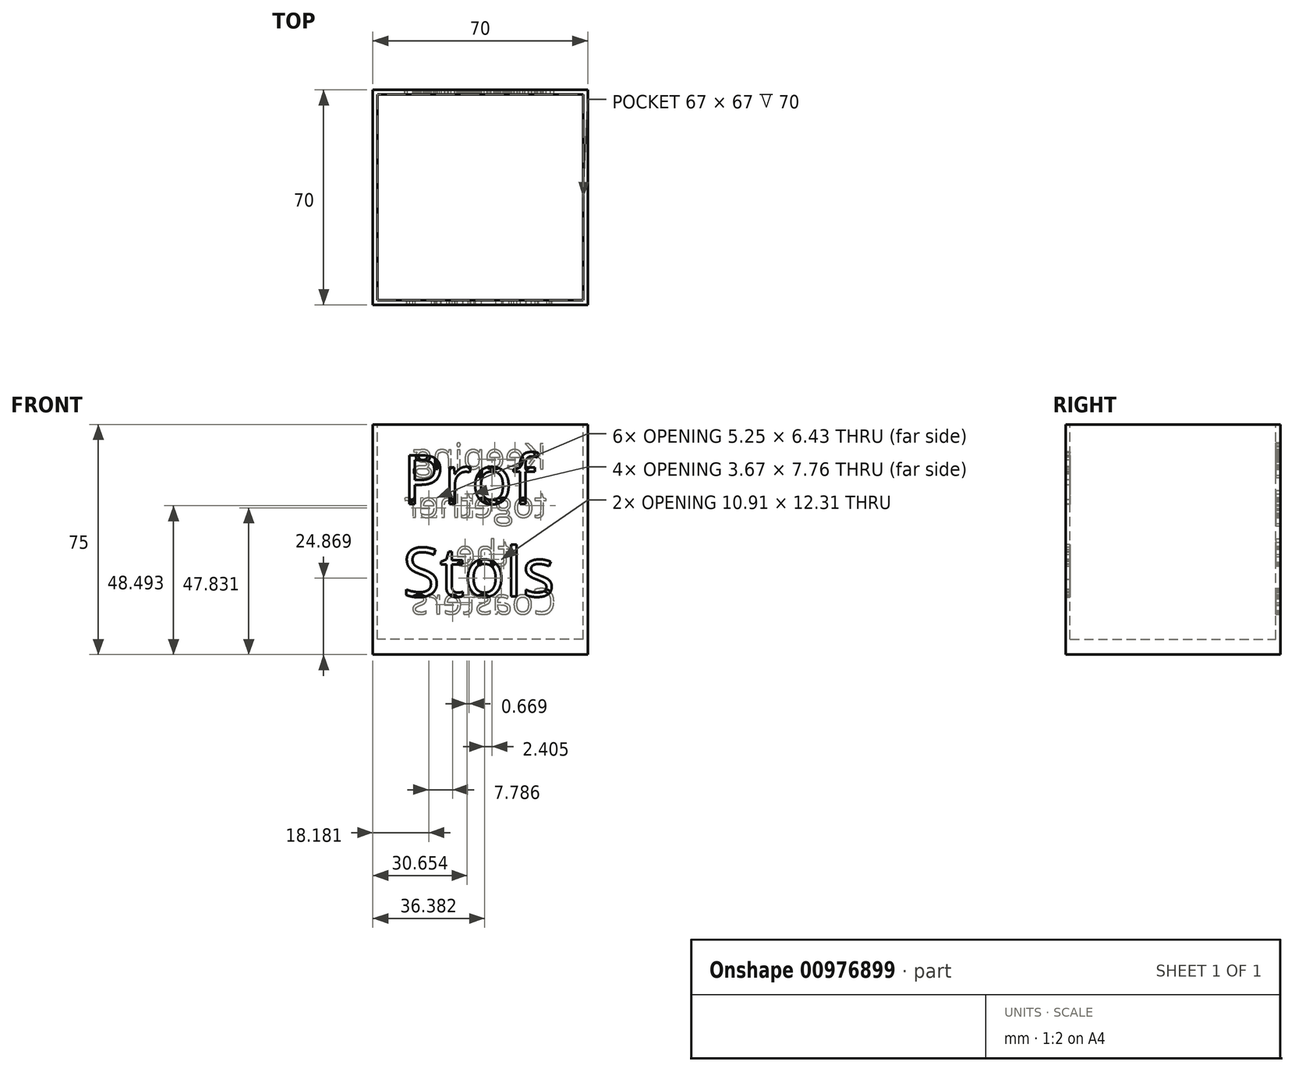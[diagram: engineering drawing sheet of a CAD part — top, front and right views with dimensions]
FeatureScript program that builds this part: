
annotation { "Feature Type Name" : "Feature", "Feature Type Description" : "" }
export const myFeature = defineFeature(function(context is Context, id is Id, definition is map)
    precondition{}
    {
        {
            var Q0;
            Q0=qCreatedBy(makeId("Top.planeOp"),FACE);
            var sketch = newSketch(context, id + "F0", { "sketchPlane" : qUnion([Q0])});
            skLineSegment(sketch, "E0.bottom", {"start": v(35, -35) * mm, "end": v(-35, -35) * mm});
            skLineSegment(sketch, "E0.top", {"start": v(35, 35) * mm, "end": v(-35, 35) * mm});
            skLineSegment(sketch, "E0.left", {"start": v(35, -35) * mm, "end": v(35, 35) * mm});
            skLineSegment(sketch, "E0.right", {"start": v(-35, -35) * mm, "end": v(-35, 35) * mm});
            skPoint(sketch, "E0.middle", {"position": v(0, 0) * mm});
            skSolve(sketch);
        }
        {
            var Q0;
            Q0 = qSketchRegion(id + "F0", true);
            extrude(context, id + "F1", {"entities" : qUnion([Q0]), "depth" : 75 * mm, "offsetDistance" : 25 * mm});
        }
        {
            var Q0;
            Q0=makeQuery(id+"F1.opExtrude","CAP_FACE",FACE,{"disambiguationData":[OSD([sQuery(id+"F0.wireOp",EDGE,"E0.bottom"),sQuery(id+"F0.wireOp",EDGE,"E0.top"),sQuery(id+"F0.wireOp",EDGE,"E0.left"),sQuery(id+"F0.wireOp",EDGE,"E0.right")])],"isStart":false});
            var sketch = newSketch(context, id + "F2", { "sketchPlane" : qUnion([Q0])});
            skLineSegment(sketch, "E1.bottom", {"start": v(33.5, -33.5) * mm, "end": v(-33.5, -33.5) * mm});
            skLineSegment(sketch, "E1.top", {"start": v(33.5, 33.5) * mm, "end": v(-33.5, 33.5) * mm});
            skLineSegment(sketch, "E1.left", {"start": v(33.5, -33.5) * mm, "end": v(33.5, 33.5) * mm});
            skLineSegment(sketch, "E1.right", {"start": v(-33.5, -33.5) * mm, "end": v(-33.5, 33.5) * mm});
            skPoint(sketch, "E1.middle", {"position": v(0, 0) * mm});
            skSolve(sketch);
        }
        {
            var Q0;
            Q0 = qSketchRegion(id + "F2", true);
            extrude(context, id + "F3", {"entities" : qUnion([Q0]), "operationType" : NewBodyOperationType.REMOVE, "oppositeDirection" : true, "depth" : 70 * mm, "offsetDistance" : 25 * mm});
        }
        {
            var Q0;
            Q0=makeQuery(id+"F1.opExtrude","SWEPT_FACE",FACE,{"disambiguationData":[OSD([sQuery(id+"F0.wireOp",EDGE,"E0.bottom")])]});
            var sketch = newSketch(context, id + "F4", { "sketchPlane" : qUnion([Q0])});
            skText(sketch, "E2", { "text": "Prof \nStols", "fontName": "OpenSans-Regular.ttf"});
            const initialGuessF4  = {"E2": [-0.02532, 0.0491, 1, 0, 0.01597]};
            skSetInitialGuess(sketch, initialGuessF4);
            skSolve(sketch);
        }
        {
            var Q0;
            Q0 = qSketchRegion(id + "F4", true);
            extrude(context, id + "F5", {"entities" : qUnion([Q0]), "operationType" : NewBodyOperationType.REMOVE, "oppositeDirection" : true, "depth" : 5 * mm, "offsetDistance" : 25 * mm});
        }
        {
            var Q0;
            Q0=makeQuery(id+"F1.opExtrude","SWEPT_FACE",FACE,{"disambiguationData":[OSD([sQuery(id+"F0.wireOp",EDGE,"E0.top")])]});
            var sketch = newSketch(context, id + "F6", { "sketchPlane" : qUnion([Q0])});
            skText(sketch, "E3", { "text": " Keeping \n together\n     the\nCoasters ", "fontName": "OpenSans-Regular.ttf"});
            const initialGuessF6  = {"E3": [-0.02464, 0.0605, 1, 0, 0.00835]};
            skSetInitialGuess(sketch, initialGuessF6);
            skSolve(sketch);
        }
        {
            var Q0;
            Q0 = qSketchRegion(id + "F6", true);
            extrude(context, id + "F7", {"entities" : qUnion([Q0]), "operationType" : NewBodyOperationType.REMOVE, "oppositeDirection" : true, "depth" : 5 * mm, "offsetDistance" : 25 * mm});
        }
    });
